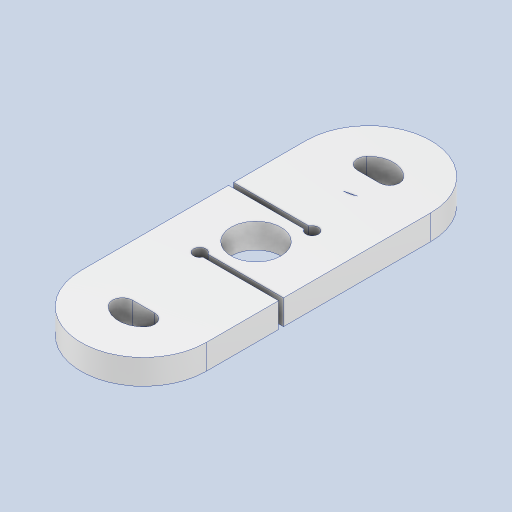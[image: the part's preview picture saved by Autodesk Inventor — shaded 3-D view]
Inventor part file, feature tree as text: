
AUTODESK INVENTOR PART (.ipt)
format: ipt  version: 2024 (Build 280153000, 153)  size: 207,872 bytes
history: native  units: mm
features: extrude x1, fillet x1, sketch x1
ambient origin geometry x8: Origin, YZ Plane, XZ Plane, XY Plane, X Axis, Y Axis, Z Axis, Center Point
bodies: Body1 (feature_tree)
feature tree (3):
  extrude  "Extrusión9"  Depth=50.0mm
  fillet  "Empalme3"  Radius=90.0mm
  sketch  "Boceto1"  dims[d42=50.0mm d43=50.0mm d44=90.0mm d45=20.0mm d46=20.0mm d47=20.0mm d48=5.0mm d49=2.0mm d50=14.0mm d51=5.0mm d52=2.0mm d53=14.0mm d54=10.0mm d55=0.0mm d56=4.0mm d16=1.0mm d17=1.0mm d18=1.0mm d19=0.15mm d20=0.25mm d21=0.375mm d22=14.3117mm d23=0.75mm d24=20.594885mm d25=0.0625mm d26=0.75mm d27=0.375mm]
